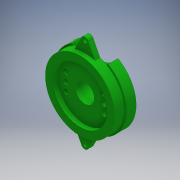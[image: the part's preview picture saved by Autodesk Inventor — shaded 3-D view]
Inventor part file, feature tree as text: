
AUTODESK INVENTOR PART (.ipt)
format: ipt  version: 2018 (Build 220112000, 112)  size: 260,608 bytes
history: native  units: mm
features: projected_geometry x12, extrude x11, sketch x11, pattern_circular x5, mirror x2
ambient origin geometry x8: Origin, YZ Plane, XZ Plane, XY Plane, X Axis, Y Axis, Z Axis, Center Point
bodies: Solid1 (feature_tree)
feature tree (41):
  extrude  "Extrusion1"  Depth=3.0mm
  extrude  "Extrusion2"  Depth=2.0mm TaperAngle=0.0deg
  extrude  "Extrusion3"  Depth=2.0mm TaperAngle=0.0deg
  extrude  "Extrusion4"  Depth=1.9mm
  pattern_circular  "Circular Pattern1"  Count=4 Angle=360.0deg
  extrude  "Extrusion5"  Depth=3.0mm
  extrude  "Extrusion6"  Depth=3.0mm
  extrude  "Extrusion7"  Depth=3.0mm
  extrude  "Extrusion8"  TaperAngle=0.0deg  [1 undecoded]
  extrude  "Extrusion9"  Depth=4.0mm
  extrude  "Extrusion10"  Depth=4.0mm
  pattern_circular  "Circular Pattern2"  [2 undecoded]
  pattern_circular  "Circular Pattern4"  [2 undecoded]
  extrude  "Extrusion11"  Depth=4.0mm TaperAngle=0.0deg
  pattern_circular  "Circular Pattern5"  [2 undecoded]
  pattern_circular  "Circular Pattern6"  [2 undecoded]
  mirror  "Mirror1"
  mirror  "Mirror2"
  sketch  "Sketch1"  dims[d0=21.5mm d1=3.0mm]
  sketch  "Sketch2"  dims[d2=1.9mm d3=0.0mm d4=2.0mm d5=0.0mm]
  sketch  "Sketch3"  dims[d6=3.5mm d7=2.0mm d8=0.0mm]
  sketch  "Sketch4"  dims[d9=1.9mm d10=1.9mm]
  sketch  "Sketch5"  dims[d11=1.9mm]
  sketch  "Sketch6"  dims[d12=7.5mm]
  sketch  "Sketch7"  dims[d13=7.5mm]
  sketch  "Sketch8"  dims[d14=7.5mm]
  projected_geometry  "Projected Loop1"
  projected_geometry  "Projected Loop2"
  projected_geometry  "Projected Loop3"
  projected_geometry  "Projected Loop4"
  projected_geometry  "Projected Loop5"
  projected_geometry  "Projected Loop6"
  projected_geometry  "Projected Loop7"
  projected_geometry  "Projected Loop8"
  projected_geometry  "Projected Loop9"
  projected_geometry  "Projected Loop10"
  projected_geometry  "Projected Loop11"
  projected_geometry  "Projected Loop12"
  sketch  "Sketch9"  dims[d15=3.4mm]
  sketch  "Sketch10"  dims[d16=3.4mm]
  sketch  "Sketch11"  dims[d17=2.0mm d18=0.0mm d19=40.0mm d20=360.0deg d22=1.6mm d23=17.85mm d24=2.9mm d25=0.0mm d26=4.0mm d27=4.0mm d28=2.0mm d29=0.0mm d30=28.7mm d31=4.0mm d32=0.0mm d33=16.57mm d34=4.0mm d35=0.0mm d36=4.0mm d37=0.0mm d38=7.5mm d39=10.0mm d40=0.0mm d41=2.1mm d42=2.1mm d43=2.1mm d44=0.0mm d45=7.5mm d46=7.5mm d47=7.5mm d48=3.4mm d49=3.4mm d50=10.0mm d51=0.0mm d52=20.0mm d53=90.0deg d58=20.0mm d59=360.0deg d61=3.3mm d62=3.3mm d63=3.3mm d64=3.0mm d65=0.0mm d66=20.0mm d67=360.0deg d69=20.0mm d70=90.0deg]
note: 9 required parameter values undecoded (feature->parameter linkage not recoverable at this tier; creation-order binding heuristic only, values carry confidence <= 0.55)
